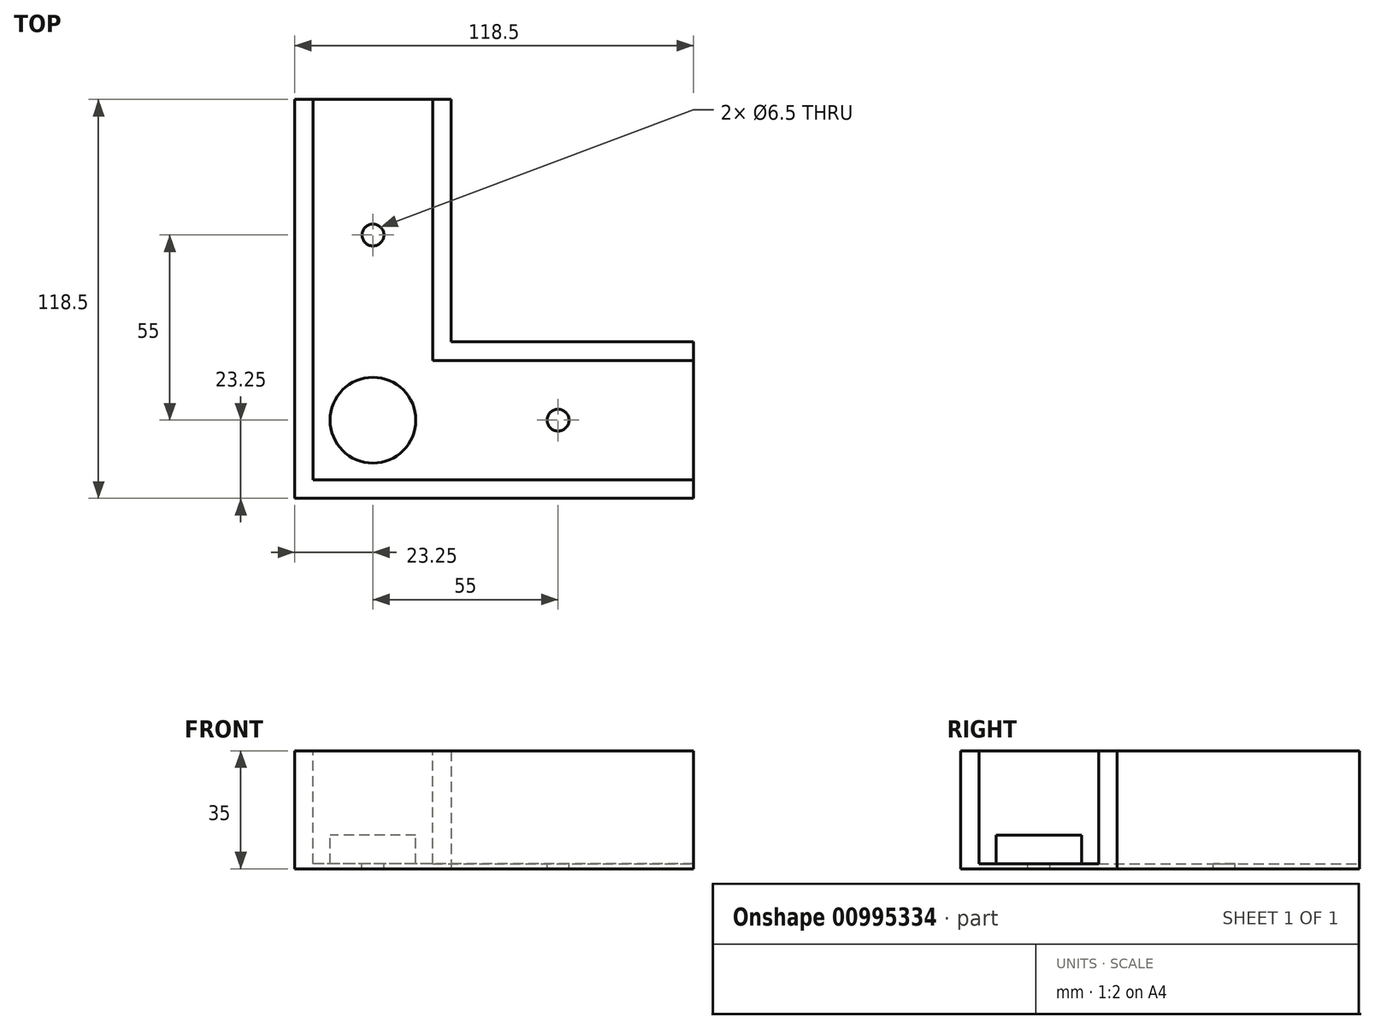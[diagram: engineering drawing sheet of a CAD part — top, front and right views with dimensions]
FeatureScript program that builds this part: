
annotation { "Feature Type Name" : "Feature", "Feature Type Description" : "" }
export const myFeature = defineFeature(function(context is Context, id is Id, definition is map)
    precondition{}
    {
        {
            var Q0;
            Q0=qCreatedBy(makeId("Top.planeOp"),FACE);
            var sketch = newSketch(context, id + "F0", { "sketchPlane" : qUnion([Q0])});
            skLineSegment(sketch, "E0.bottom", {"start": v(0, 0) * mm, "end": v(72, 0) * mm});
            skLineSegment(sketch, "E0.top", {"start": v(0, -46.5) * mm, "end": v(72, -46.5) * mm});
            skLineSegment(sketch, "E0.right", {"start": v(72, 0) * mm, "end": v(72, -46.5) * mm});
            skLineSegment(sketch, "E1.bottom", {"start": v(0, -46.5) * mm, "end": v(-46.5, -46.5) * mm});
            skLineSegment(sketch, "E1.top", {"start": v(0, 72) * mm, "end": v(-46.5, 72) * mm});
            skLineSegment(sketch, "E1.left", {"start": v(0, 0) * mm, "end": v(0, 72) * mm});
            skLineSegment(sketch, "E1.right", {"start": v(-46.5, -46.5) * mm, "end": v(-46.5, 72) * mm});
            skSolve(sketch);
        }
        {
            var Q0;
            Q0=makeQuery(id+"F0.imprint","IMPRINT",FACE,{"disambiguationData":[TD([[makeQuery(id+"F0.imprint","IMPRINT",EDGE,{"derivedFrom":sQuery(id+"F0.wireOp",EDGE,"E0.bottom")}),-1.0]])]});
            extrude(context, id + "F1", {"entities" : qUnion([Q0]), "depth" : 35 * mm, "offsetDistance" : 25 * mm});
        }
        {
            var Q0;
            Q0=makeQuery(id+"F1.opExtrude","CAP_FACE",FACE,{"disambiguationData":[OSD([sQuery(id+"F0.wireOp",EDGE,"E0.bottom"),sQuery(id+"F0.wireOp",EDGE,"E0.top"),sQuery(id+"F0.wireOp",EDGE,"E0.right"),sQuery(id+"F0.wireOp",EDGE,"E1.bottom"),sQuery(id+"F0.wireOp",EDGE,"E1.top"),sQuery(id+"F0.wireOp",EDGE,"E1.left"),sQuery(id+"F0.wireOp",EDGE,"E1.right")])],"isStart":false});
            var sketch = newSketch(context, id + "F2", { "sketchPlane" : qUnion([Q0])});
            skLineSegment(sketch, "E2.0", {"start": v(-41, -41) * mm, "end": v(-41, 72) * mm});
            skLineSegment(sketch, "E2.1", {"start": v(72, -41) * mm, "end": v(-41, -41) * mm});
            skLineSegment(sketch, "E3.0", {"start": v(-5.5, -5.5) * mm, "end": v(-5.5, 72) * mm});
            skLineSegment(sketch, "E3.1", {"start": v(-5.5, -5.5) * mm, "end": v(72, -5.5) * mm});
            skSolve(sketch);
        }
        {
            var Q0;
            {var subQ2=sQuery(id+"F2.wireOp",EDGE,"E2.0");Q0=makeQuery(id+"F2.imprint","IMPRINT",FACE,{"disambiguationData":[TD([[makeQuery(id+"F2.imprint","IMPRINT",EDGE,{"derivedFrom":subQ2}),-1.0]])]});}
            extrude(context, id + "F3", {"entities" : qUnion([Q0]), "operationType" : NewBodyOperationType.REMOVE, "oppositeDirection" : true, "depth" : 25 * mm, "offsetDistance" : 25 * mm});
        }
        {
            var Q0;
            Q0=makeQuery(id+"F3.boolean.opBoolean","COPY",FACE,{"derivedFrom":makeQuery(id+"F3.opExtrude","CAP_FACE",FACE,{"disambiguationData":[OSD([sQuery(id+"F0.wireOp",EDGE,"E0.right"),sQuery(id+"F0.wireOp",EDGE,"E1.top"),sQuery(id+"F2.wireOp",EDGE,"E2.0"),sQuery(id+"F2.wireOp",EDGE,"E2.1"),sQuery(id+"F2.wireOp",EDGE,"E3.0"),sQuery(id+"F2.wireOp",EDGE,"E3.1")])],"isStart":false})});
            var sketch = newSketch(context, id + "F4", { "sketchPlane" : qUnion([Q0])});
            skLineSegment(sketch, "E4", {"start": v(-41, -41) * mm, "end": v(-5.5, -5.5) * mm});
            skCircle(sketch, "E5", {"center": v(-23.25, -23.25) * mm, "radius": 12.75 * mm});
            skPoint(sketch, "E6", {"position": v(31.75, -23.25) * mm});
            skPoint(sketch, "E7", {"position": v(-23.25, 31.75) * mm});
            skSolve(sketch);
        }
        {
            var Q0;
            {var subQ0=sQuery(id+"F4.wireOp",EDGE,"E5");var subQ1=sQuery(id+"F4.wireOp",EDGE,"E4");var subQ2=makeQuery(id+"F4.imprint","INTERSECT",VERTEX,{"disambiguationData":[OD(0.0)],"derivedFrom":[subQ1,subQ0]});Q0=makeQuery(id+"F4.imprint","IMPRINT",FACE,{"disambiguationData":[TD([[makeQuery(id+"F4.imprint","IMPRINT",EDGE,{"disambiguationData":[TD([[subQ2,-1.0]])],"derivedFrom":subQ1}),-1.0]])]});}
            var Q1;
            {var subQ0=sQuery(id+"F4.wireOp",EDGE,"E5");var subQ1=sQuery(id+"F4.wireOp",EDGE,"E4");var subQ2=makeQuery(id+"F4.imprint","INTERSECT",VERTEX,{"disambiguationData":[OD(0.0)],"derivedFrom":[subQ1,subQ0]});Q1=makeQuery(id+"F4.imprint","IMPRINT",FACE,{"disambiguationData":[TD([[makeQuery(id+"F4.imprint","IMPRINT",EDGE,{"disambiguationData":[TD([[subQ2,-1.0]])],"derivedFrom":subQ1}),1.0]])]});}
            var Q2;
            Q2=sQuery(id+"F4.wireOp",EDGE,"E5");
            extrude(context, id + "F5", {"entities" : qUnion([Q0, Q1]), "operationType" : NewBodyOperationType.REMOVE, "surfaceEntities" : qUnion([Q2]), "oppositeDirection" : true, "depth" : 8.5 * mm, "offsetDistance" : 25 * mm});
        }
        {
            var Q0;
            Q0=sQuery(id+"F4.wireOp",VERTEX,"E6");
            var Q1;
            Q1=sQuery(id+"F4.wireOp",VERTEX,"E7");
            var Q2;
            Q2=makeQuery(id+"F1.opExtrude","SWEPT_BODY",BODY,{"disambiguationData":[OSD([sQuery(id+"F0.wireOp",EDGE,"E0.bottom"),sQuery(id+"F0.wireOp",EDGE,"E0.top"),sQuery(id+"F0.wireOp",EDGE,"E0.right"),sQuery(id+"F0.wireOp",EDGE,"E1.bottom"),sQuery(id+"F0.wireOp",EDGE,"E1.top"),sQuery(id+"F0.wireOp",EDGE,"E1.left"),sQuery(id+"F0.wireOp",EDGE,"E1.right")])]});
            hole(context, id + "F6", {"style" : HoleStyle.SIMPLE, "endStyle" : HoleEndStyle.BLIND, "holeDiameter" : 6.5 * mm, "majorDiameter" : 5 * mm, "holeDepth" : 5 * mm, "isTappedThrough" : true, "tappedDepth" : 12 * mm, "tapClearance" : 3, "locations" : qUnion([Q0, Q1]), "scope" : qUnion([Q2])});
        }
    });
